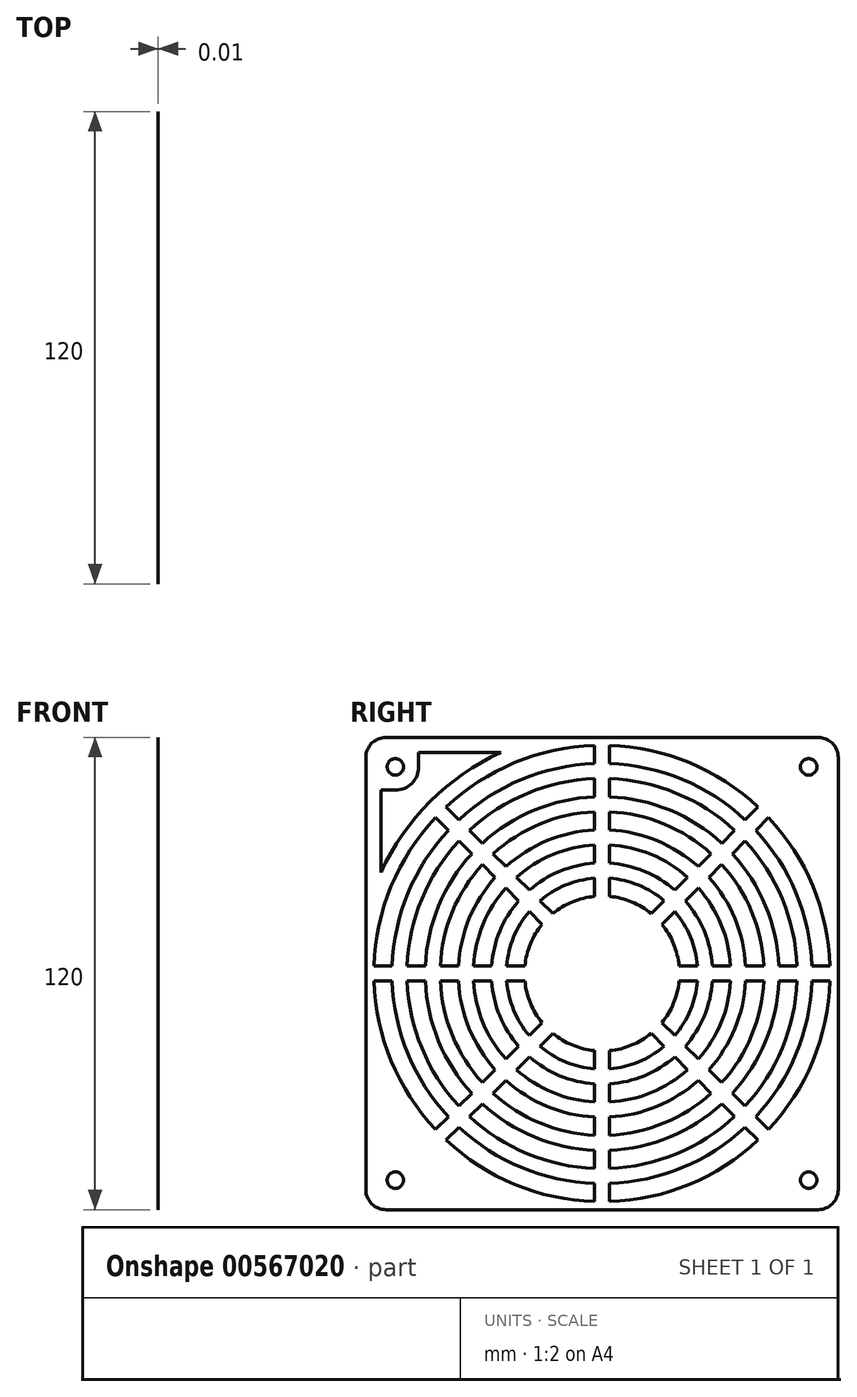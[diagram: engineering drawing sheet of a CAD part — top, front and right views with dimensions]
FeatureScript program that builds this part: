
annotation { "Feature Type Name" : "Feature", "Feature Type Description" : "" }
export const myFeature = defineFeature(function(context is Context, id is Id, definition is map)
    precondition{}
    {
        {
            var Q0;
            Q0=qCreatedBy(makeId("Right.planeOp"),FACE);
            var sketch = newSketch(context, id + "F0", { "sketchPlane" : qUnion([Q0])});
            skLineSegment(sketch, "E0.bottom", {"start": v(-54.92, 60) * mm, "end": v(54.92, 60) * mm});
            skLineSegment(sketch, "E0.top", {"start": v(-54.92, -60) * mm, "end": v(54.92, -60) * mm});
            skLineSegment(sketch, "E0.left", {"start": v(-60, 54.92) * mm, "end": v(-60, -54.92) * mm});
            skLineSegment(sketch, "E0.right", {"start": v(60, 54.92) * mm, "end": v(60, -54.92) * mm});
            skPoint(sketch, "E0.middle", {"position": v(0, 0) * mm});
            skPoint(sketch, "E1.visualSharp", {"position": v(-60, 60) * mm});
            skArc(sketch, "E1.filletArc", {"start": v(-54.92, 60) * mm, "mid": v(-58.51, 58.51) * mm, "end": v(-60, 54.92) * mm});
            skPoint(sketch, "E2.visualSharp", {"position": v(60, 60) * mm});
            skArc(sketch, "E2.filletArc", {"start": v(60, 54.92) * mm, "mid": v(58.51, 58.51) * mm, "end": v(54.92, 60) * mm});
            skPoint(sketch, "E3.visualSharp", {"position": v(60, -60) * mm});
            skArc(sketch, "E3.filletArc", {"start": v(54.92, -60) * mm, "mid": v(58.51, -58.51) * mm, "end": v(60, -54.92) * mm});
            skPoint(sketch, "E4.visualSharp", {"position": v(-60, -60) * mm});
            skArc(sketch, "E4.filletArc", {"start": v(-60, -54.92) * mm, "mid": v(-58.51, -58.51) * mm, "end": v(-54.92, -60) * mm});
            skLineSegment(sketch, "E5.bottom", {"start": v(-52.5, 52.5) * mm, "end": v(52.5, 52.5) * mm, "construction": true});
            skLineSegment(sketch, "E5.top", {"start": v(-52.5, -52.5) * mm, "end": v(52.5, -52.5) * mm, "construction": true});
            skLineSegment(sketch, "E5.left", {"start": v(-52.5, 52.5) * mm, "end": v(-52.5, -52.5) * mm, "construction": true});
            skLineSegment(sketch, "E5.right", {"start": v(52.5, 52.5) * mm, "end": v(52.5, -52.5) * mm, "construction": true});
            skCircle(sketch, "E6", {"center": v(-52.5, 52.5) * mm, "radius": 2.1 * mm});
            skCircle(sketch, "E7", {"center": v(52.5, 52.5) * mm, "radius": 2.1 * mm});
            skCircle(sketch, "E8", {"center": v(52.5, -52.5) * mm, "radius": 2.1 * mm});
            skCircle(sketch, "E9", {"center": v(-52.5, -52.5) * mm, "radius": 2.1 * mm});
            skCircle(sketch, "E10", {"center": v(0, 0) * mm, "radius": 57.98 * mm});
            skCircle(sketch, "E11", {"center": v(0, 0) * mm, "radius": 19.69 * mm});
            skCircle(sketch, "E12", {"center": v(0, 0) * mm, "radius": 24.3 * mm});
            skCircle(sketch, "E13", {"center": v(0, 0) * mm, "radius": 28.1 * mm});
            skCircle(sketch, "E14", {"center": v(0, 0) * mm, "radius": 32.72 * mm});
            skCircle(sketch, "E15", {"center": v(0, 0) * mm, "radius": 36.53 * mm});
            skCircle(sketch, "E16", {"center": v(0, 0) * mm, "radius": 41.14 * mm});
            skCircle(sketch, "E17", {"center": v(0, 0) * mm, "radius": 44.95 * mm});
            skLineSegment(sketch, "E18", {"start": v(0, 19.69) * mm, "end": v(0, 24.3) * mm, "construction": true});
            skLineSegment(sketch, "E19", {"start": v(0, 24.3) * mm, "end": v(0, 28.1) * mm, "construction": true});
            skLineSegment(sketch, "E20", {"start": v(0, 28.1) * mm, "end": v(0, 32.72) * mm, "construction": true});
            skLineSegment(sketch, "E21", {"start": v(0, 32.72) * mm, "end": v(0, 36.53) * mm, "construction": true});
            skLineSegment(sketch, "E22", {"start": v(0, 36.53) * mm, "end": v(0, 41.14) * mm, "construction": true});
            skLineSegment(sketch, "E23", {"start": v(0, 41.14) * mm, "end": v(0, 44.95) * mm, "construction": true});
            skCircle(sketch, "E24", {"center": v(0, 0) * mm, "radius": 49.56 * mm});
            skCircle(sketch, "E25", {"center": v(0, 0) * mm, "radius": 53.37 * mm});
            skLineSegment(sketch, "E26", {"start": v(0, 44.95) * mm, "end": v(0, 49.56) * mm, "construction": true});
            skLineSegment(sketch, "E27", {"start": v(0, 49.56) * mm, "end": v(0, 53.37) * mm, "construction": true});
            skLineSegment(sketch, "E28", {"start": v(0, 53.37) * mm, "end": v(0, 57.98) * mm, "construction": true});
            skLineSegment(sketch, "E29", {"start": v(-19.6, 1.9) * mm, "end": v(-57.94, 1.9) * mm});
            skLineSegment(sketch, "E30", {"start": v(-57.94, -1.9) * mm, "end": v(-19.6, -1.9) * mm});
            skLineSegment(sketch, "E31", {"start": v(-38.77, 1.9) * mm, "end": v(-38.77, -1.9) * mm, "construction": true});
            skLineSegment(sketch, "E32", {"start": v(-38.77, 0) * mm, "end": v(0, 0) * mm, "construction": true});
            skLineSegment(sketch, "E33.1.0", {"start": v(-15.2, -12.5) * mm, "end": v(-42.32, -39.63) * mm});
            skLineSegment(sketch, "E33.1.1", {"start": v(-39.63, -42.32) * mm, "end": v(-12.5, -15.2) * mm});
            skLineSegment(sketch, "E33.2.0", {"start": v(-1.9, -19.6) * mm, "end": v(-1.9, -57.94) * mm});
            skLineSegment(sketch, "E33.2.1", {"start": v(1.9, -57.94) * mm, "end": v(1.9, -19.6) * mm});
            skLineSegment(sketch, "E33.3.0", {"start": v(12.5, -15.2) * mm, "end": v(39.63, -42.32) * mm});
            skLineSegment(sketch, "E33.3.1", {"start": v(42.32, -39.63) * mm, "end": v(15.2, -12.5) * mm});
            skLineSegment(sketch, "E33.4.0", {"start": v(19.6, -1.9) * mm, "end": v(57.94, -1.9) * mm});
            skLineSegment(sketch, "E33.4.1", {"start": v(57.94, 1.9) * mm, "end": v(19.6, 1.9) * mm});
            skLineSegment(sketch, "E33.5.0", {"start": v(15.2, 12.5) * mm, "end": v(42.32, 39.63) * mm});
            skLineSegment(sketch, "E33.5.1", {"start": v(39.63, 42.32) * mm, "end": v(12.5, 15.2) * mm});
            skLineSegment(sketch, "E33.6.0", {"start": v(1.9, 19.6) * mm, "end": v(1.9, 57.94) * mm});
            skLineSegment(sketch, "E33.6.1", {"start": v(-1.9, 57.94) * mm, "end": v(-1.9, 19.6) * mm});
            skLineSegment(sketch, "E33.7.0", {"start": v(-12.5, 15.2) * mm, "end": v(-39.63, 42.32) * mm});
            skLineSegment(sketch, "E33.7.1", {"start": v(-42.32, 39.63) * mm, "end": v(-15.2, 12.5) * mm});
            skSolve(sketch);
        }
        {
            var Q0;
            {var subQ0=sQuery(id+"F0.wireOp",EDGE,"E33.1.0");var subQ1=sQuery(id+"F0.wireOp",EDGE,"E11");var subQ2=makeQuery(id+"F0.imprint","INTERSECT",VERTEX,{"derivedFrom":[subQ1,subQ0]});Q0=makeQuery(id+"F0.imprint","IMPRINT",FACE,{"disambiguationData":[TD([[makeQuery(id+"F0.imprint","IMPRINT",EDGE,{"disambiguationData":[TD([[subQ2,-1.0]])],"derivedFrom":subQ1}),-1.0]])]});}
            var Q1;
            {var subQ0=sQuery(id+"F0.wireOp",EDGE,"E11");var subQ8=makeQuery(id+"F0.imprint","INTERSECT",VERTEX,{"derivedFrom":[subQ0,sQuery(id+"F0.wireOp",EDGE,"E33.4.1")]});Q1=makeQuery(id+"F0.imprint","IMPRINT",FACE,{"disambiguationData":[TD([[makeQuery(id+"F0.imprint","IMPRINT",EDGE,{"disambiguationData":[TD([[subQ8,-1.0]])],"derivedFrom":subQ0}),1.0]])]});}
            var Q2;
            {var subQ0=sQuery(id+"F0.wireOp",EDGE,"E33.1.0");var subQ1=sQuery(id+"F0.wireOp",EDGE,"E12");var subQ2=makeQuery(id+"F0.imprint","INTERSECT",VERTEX,{"derivedFrom":[subQ1,subQ0]});Q2=makeQuery(id+"F0.imprint","IMPRINT",FACE,{"disambiguationData":[TD([[makeQuery(id+"F0.imprint","IMPRINT",EDGE,{"disambiguationData":[TD([[subQ2,-1.0]])],"derivedFrom":subQ1}),-1.0]])]});}
            var Q3;
            {var subQ0=sQuery(id+"F0.wireOp",EDGE,"E33.1.0");var subQ1=sQuery(id+"F0.wireOp",EDGE,"E13");var subQ2=makeQuery(id+"F0.imprint","INTERSECT",VERTEX,{"derivedFrom":[subQ1,subQ0]});Q3=makeQuery(id+"F0.imprint","IMPRINT",FACE,{"disambiguationData":[TD([[makeQuery(id+"F0.imprint","IMPRINT",EDGE,{"disambiguationData":[TD([[subQ2,-1.0]])],"derivedFrom":subQ1}),-1.0]])]});}
            var Q4;
            {var subQ0=sQuery(id+"F0.wireOp",EDGE,"E33.1.0");var subQ1=sQuery(id+"F0.wireOp",EDGE,"E14");var subQ2=makeQuery(id+"F0.imprint","INTERSECT",VERTEX,{"derivedFrom":[subQ1,subQ0]});Q4=makeQuery(id+"F0.imprint","IMPRINT",FACE,{"disambiguationData":[TD([[makeQuery(id+"F0.imprint","IMPRINT",EDGE,{"disambiguationData":[TD([[subQ2,-1.0]])],"derivedFrom":subQ1}),-1.0]])]});}
            var Q5;
            {var subQ0=sQuery(id+"F0.wireOp",EDGE,"E33.1.0");var subQ1=sQuery(id+"F0.wireOp",EDGE,"E15");var subQ2=makeQuery(id+"F0.imprint","INTERSECT",VERTEX,{"derivedFrom":[subQ1,subQ0]});Q5=makeQuery(id+"F0.imprint","IMPRINT",FACE,{"disambiguationData":[TD([[makeQuery(id+"F0.imprint","IMPRINT",EDGE,{"disambiguationData":[TD([[subQ2,-1.0]])],"derivedFrom":subQ1}),-1.0]])]});}
            var Q6;
            {var subQ0=sQuery(id+"F0.wireOp",EDGE,"E33.1.0");var subQ1=sQuery(id+"F0.wireOp",EDGE,"E16");var subQ2=makeQuery(id+"F0.imprint","INTERSECT",VERTEX,{"derivedFrom":[subQ1,subQ0]});Q6=makeQuery(id+"F0.imprint","IMPRINT",FACE,{"disambiguationData":[TD([[makeQuery(id+"F0.imprint","IMPRINT",EDGE,{"disambiguationData":[TD([[subQ2,-1.0]])],"derivedFrom":subQ1}),-1.0]])]});}
            var Q7;
            {var subQ0=sQuery(id+"F0.wireOp",EDGE,"E33.1.0");var subQ1=sQuery(id+"F0.wireOp",EDGE,"E17");var subQ2=makeQuery(id+"F0.imprint","INTERSECT",VERTEX,{"derivedFrom":[subQ1,subQ0]});Q7=makeQuery(id+"F0.imprint","IMPRINT",FACE,{"disambiguationData":[TD([[makeQuery(id+"F0.imprint","IMPRINT",EDGE,{"disambiguationData":[TD([[subQ2,-1.0]])],"derivedFrom":subQ1}),-1.0]])]});}
            var Q8;
            {var subQ0=sQuery(id+"F0.wireOp",EDGE,"E33.1.0");var subQ1=sQuery(id+"F0.wireOp",EDGE,"E24");var subQ2=makeQuery(id+"F0.imprint","INTERSECT",VERTEX,{"derivedFrom":[subQ1,subQ0]});Q8=makeQuery(id+"F0.imprint","IMPRINT",FACE,{"disambiguationData":[TD([[makeQuery(id+"F0.imprint","IMPRINT",EDGE,{"disambiguationData":[TD([[subQ2,-1.0]])],"derivedFrom":subQ1}),-1.0]])]});}
            var Q9;
            {var subQ0=sQuery(id+"F0.wireOp",EDGE,"E33.1.0");var subQ1=sQuery(id+"F0.wireOp",EDGE,"E10");var subQ2=makeQuery(id+"F0.imprint","INTERSECT",VERTEX,{"derivedFrom":[subQ1,subQ0]});Q9=makeQuery(id+"F0.imprint","IMPRINT",FACE,{"disambiguationData":[TD([[makeQuery(id+"F0.imprint","IMPRINT",EDGE,{"disambiguationData":[TD([[subQ2,-1.0]])],"derivedFrom":subQ1}),1.0]])]});}
            var Q10;
            Q10=makeQuery(id+"F0.imprint","IMPRINT",FACE,{"disambiguationData":[TD([[makeQuery(id+"F0.imprint","IMPRINT",EDGE,{"derivedFrom":sQuery(id+"F0.wireOp",EDGE,"E0.bottom")}),-1.0]])]});
            var Q11;
            {var subQ0=sQuery(id+"F0.wireOp",EDGE,"E33.2.0");var subQ1=sQuery(id+"F0.wireOp",EDGE,"E10");var subQ2=makeQuery(id+"F0.imprint","INTERSECT",VERTEX,{"derivedFrom":[subQ1,subQ0]});Q11=makeQuery(id+"F0.imprint","IMPRINT",FACE,{"disambiguationData":[TD([[makeQuery(id+"F0.imprint","IMPRINT",EDGE,{"disambiguationData":[TD([[subQ2,-1.0]])],"derivedFrom":subQ1}),1.0]])]});}
            var Q12;
            {var subQ0=sQuery(id+"F0.wireOp",EDGE,"E33.2.0");var subQ1=sQuery(id+"F0.wireOp",EDGE,"E24");var subQ2=makeQuery(id+"F0.imprint","INTERSECT",VERTEX,{"derivedFrom":[subQ1,subQ0]});Q12=makeQuery(id+"F0.imprint","IMPRINT",FACE,{"disambiguationData":[TD([[makeQuery(id+"F0.imprint","IMPRINT",EDGE,{"disambiguationData":[TD([[subQ2,-1.0]])],"derivedFrom":subQ1}),-1.0]])]});}
            var Q13;
            {var subQ0=sQuery(id+"F0.wireOp",EDGE,"E33.2.0");var subQ1=sQuery(id+"F0.wireOp",EDGE,"E17");var subQ2=makeQuery(id+"F0.imprint","INTERSECT",VERTEX,{"derivedFrom":[subQ1,subQ0]});Q13=makeQuery(id+"F0.imprint","IMPRINT",FACE,{"disambiguationData":[TD([[makeQuery(id+"F0.imprint","IMPRINT",EDGE,{"disambiguationData":[TD([[subQ2,-1.0]])],"derivedFrom":subQ1}),-1.0]])]});}
            var Q14;
            {var subQ0=sQuery(id+"F0.wireOp",EDGE,"E33.2.0");var subQ1=sQuery(id+"F0.wireOp",EDGE,"E16");var subQ2=makeQuery(id+"F0.imprint","INTERSECT",VERTEX,{"derivedFrom":[subQ1,subQ0]});Q14=makeQuery(id+"F0.imprint","IMPRINT",FACE,{"disambiguationData":[TD([[makeQuery(id+"F0.imprint","IMPRINT",EDGE,{"disambiguationData":[TD([[subQ2,-1.0]])],"derivedFrom":subQ1}),-1.0]])]});}
            var Q15;
            {var subQ0=sQuery(id+"F0.wireOp",EDGE,"E33.2.0");var subQ1=sQuery(id+"F0.wireOp",EDGE,"E15");var subQ2=makeQuery(id+"F0.imprint","INTERSECT",VERTEX,{"derivedFrom":[subQ1,subQ0]});Q15=makeQuery(id+"F0.imprint","IMPRINT",FACE,{"disambiguationData":[TD([[makeQuery(id+"F0.imprint","IMPRINT",EDGE,{"disambiguationData":[TD([[subQ2,-1.0]])],"derivedFrom":subQ1}),-1.0]])]});}
            var Q16;
            {var subQ0=sQuery(id+"F0.wireOp",EDGE,"E33.2.0");var subQ1=sQuery(id+"F0.wireOp",EDGE,"E14");var subQ2=makeQuery(id+"F0.imprint","INTERSECT",VERTEX,{"derivedFrom":[subQ1,subQ0]});Q16=makeQuery(id+"F0.imprint","IMPRINT",FACE,{"disambiguationData":[TD([[makeQuery(id+"F0.imprint","IMPRINT",EDGE,{"disambiguationData":[TD([[subQ2,-1.0]])],"derivedFrom":subQ1}),-1.0]])]});}
            var Q17;
            {var subQ0=sQuery(id+"F0.wireOp",EDGE,"E33.2.0");var subQ1=sQuery(id+"F0.wireOp",EDGE,"E13");var subQ2=makeQuery(id+"F0.imprint","INTERSECT",VERTEX,{"derivedFrom":[subQ1,subQ0]});Q17=makeQuery(id+"F0.imprint","IMPRINT",FACE,{"disambiguationData":[TD([[makeQuery(id+"F0.imprint","IMPRINT",EDGE,{"disambiguationData":[TD([[subQ2,-1.0]])],"derivedFrom":subQ1}),-1.0]])]});}
            var Q18;
            {var subQ0=sQuery(id+"F0.wireOp",EDGE,"E33.2.0");var subQ1=sQuery(id+"F0.wireOp",EDGE,"E12");var subQ2=makeQuery(id+"F0.imprint","INTERSECT",VERTEX,{"derivedFrom":[subQ1,subQ0]});Q18=makeQuery(id+"F0.imprint","IMPRINT",FACE,{"disambiguationData":[TD([[makeQuery(id+"F0.imprint","IMPRINT",EDGE,{"disambiguationData":[TD([[subQ2,-1.0]])],"derivedFrom":subQ1}),-1.0]])]});}
            var Q19;
            {var subQ0=sQuery(id+"F0.wireOp",EDGE,"E33.2.0");var subQ1=sQuery(id+"F0.wireOp",EDGE,"E11");var subQ2=makeQuery(id+"F0.imprint","INTERSECT",VERTEX,{"derivedFrom":[subQ1,subQ0]});Q19=makeQuery(id+"F0.imprint","IMPRINT",FACE,{"disambiguationData":[TD([[makeQuery(id+"F0.imprint","IMPRINT",EDGE,{"disambiguationData":[TD([[subQ2,-1.0]])],"derivedFrom":subQ1}),-1.0]])]});}
            var Q20;
            {var subQ0=sQuery(id+"F0.wireOp",EDGE,"E33.1.1");var subQ1=sQuery(id+"F0.wireOp",EDGE,"E12");var subQ2=makeQuery(id+"F0.imprint","INTERSECT",VERTEX,{"derivedFrom":[subQ1,subQ0]});Q20=makeQuery(id+"F0.imprint","IMPRINT",FACE,{"disambiguationData":[TD([[makeQuery(id+"F0.imprint","IMPRINT",EDGE,{"disambiguationData":[TD([[subQ2,-1.0]])],"derivedFrom":subQ1}),-1.0]])]});}
            var Q21;
            {var subQ0=sQuery(id+"F0.wireOp",EDGE,"E33.1.1");var subQ1=sQuery(id+"F0.wireOp",EDGE,"E14");var subQ2=makeQuery(id+"F0.imprint","INTERSECT",VERTEX,{"derivedFrom":[subQ1,subQ0]});Q21=makeQuery(id+"F0.imprint","IMPRINT",FACE,{"disambiguationData":[TD([[makeQuery(id+"F0.imprint","IMPRINT",EDGE,{"disambiguationData":[TD([[subQ2,-1.0]])],"derivedFrom":subQ1}),-1.0]])]});}
            var Q22;
            {var subQ0=sQuery(id+"F0.wireOp",EDGE,"E33.1.1");var subQ1=sQuery(id+"F0.wireOp",EDGE,"E16");var subQ2=makeQuery(id+"F0.imprint","INTERSECT",VERTEX,{"derivedFrom":[subQ1,subQ0]});Q22=makeQuery(id+"F0.imprint","IMPRINT",FACE,{"disambiguationData":[TD([[makeQuery(id+"F0.imprint","IMPRINT",EDGE,{"disambiguationData":[TD([[subQ2,-1.0]])],"derivedFrom":subQ1}),-1.0]])]});}
            var Q23;
            {var subQ0=sQuery(id+"F0.wireOp",EDGE,"E33.1.1");var subQ1=sQuery(id+"F0.wireOp",EDGE,"E24");var subQ2=makeQuery(id+"F0.imprint","INTERSECT",VERTEX,{"derivedFrom":[subQ1,subQ0]});Q23=makeQuery(id+"F0.imprint","IMPRINT",FACE,{"disambiguationData":[TD([[makeQuery(id+"F0.imprint","IMPRINT",EDGE,{"disambiguationData":[TD([[subQ2,-1.0]])],"derivedFrom":subQ1}),-1.0]])]});}
            var Q24;
            {var subQ0=sQuery(id+"F0.wireOp",EDGE,"E33.2.1");var subQ1=sQuery(id+"F0.wireOp",EDGE,"E24");var subQ2=makeQuery(id+"F0.imprint","INTERSECT",VERTEX,{"derivedFrom":[subQ1,subQ0]});Q24=makeQuery(id+"F0.imprint","IMPRINT",FACE,{"disambiguationData":[TD([[makeQuery(id+"F0.imprint","IMPRINT",EDGE,{"disambiguationData":[TD([[subQ2,-1.0]])],"derivedFrom":subQ1}),-1.0]])]});}
            var Q25;
            {var subQ0=sQuery(id+"F0.wireOp",EDGE,"E33.2.1");var subQ1=sQuery(id+"F0.wireOp",EDGE,"E16");var subQ2=makeQuery(id+"F0.imprint","INTERSECT",VERTEX,{"derivedFrom":[subQ1,subQ0]});Q25=makeQuery(id+"F0.imprint","IMPRINT",FACE,{"disambiguationData":[TD([[makeQuery(id+"F0.imprint","IMPRINT",EDGE,{"disambiguationData":[TD([[subQ2,-1.0]])],"derivedFrom":subQ1}),-1.0]])]});}
            var Q26;
            {var subQ0=sQuery(id+"F0.wireOp",EDGE,"E33.2.1");var subQ1=sQuery(id+"F0.wireOp",EDGE,"E14");var subQ2=makeQuery(id+"F0.imprint","INTERSECT",VERTEX,{"derivedFrom":[subQ1,subQ0]});Q26=makeQuery(id+"F0.imprint","IMPRINT",FACE,{"disambiguationData":[TD([[makeQuery(id+"F0.imprint","IMPRINT",EDGE,{"disambiguationData":[TD([[subQ2,-1.0]])],"derivedFrom":subQ1}),-1.0]])]});}
            var Q27;
            {var subQ0=sQuery(id+"F0.wireOp",EDGE,"E33.2.1");var subQ1=sQuery(id+"F0.wireOp",EDGE,"E12");var subQ2=makeQuery(id+"F0.imprint","INTERSECT",VERTEX,{"derivedFrom":[subQ1,subQ0]});Q27=makeQuery(id+"F0.imprint","IMPRINT",FACE,{"disambiguationData":[TD([[makeQuery(id+"F0.imprint","IMPRINT",EDGE,{"disambiguationData":[TD([[subQ2,-1.0]])],"derivedFrom":subQ1}),-1.0]])]});}
            var Q28;
            {var subQ0=sQuery(id+"F0.wireOp",EDGE,"E33.3.0");var subQ1=sQuery(id+"F0.wireOp",EDGE,"E12");var subQ2=makeQuery(id+"F0.imprint","INTERSECT",VERTEX,{"derivedFrom":[subQ1,subQ0]});Q28=makeQuery(id+"F0.imprint","IMPRINT",FACE,{"disambiguationData":[TD([[makeQuery(id+"F0.imprint","IMPRINT",EDGE,{"disambiguationData":[TD([[subQ2,-1.0]])],"derivedFrom":subQ1}),-1.0]])]});}
            var Q29;
            {var subQ0=sQuery(id+"F0.wireOp",EDGE,"E33.3.0");var subQ1=sQuery(id+"F0.wireOp",EDGE,"E11");var subQ2=makeQuery(id+"F0.imprint","INTERSECT",VERTEX,{"derivedFrom":[subQ1,subQ0]});Q29=makeQuery(id+"F0.imprint","IMPRINT",FACE,{"disambiguationData":[TD([[makeQuery(id+"F0.imprint","IMPRINT",EDGE,{"disambiguationData":[TD([[subQ2,-1.0]])],"derivedFrom":subQ1}),-1.0]])]});}
            var Q30;
            {var subQ0=sQuery(id+"F0.wireOp",EDGE,"E33.3.0");var subQ1=sQuery(id+"F0.wireOp",EDGE,"E13");var subQ2=makeQuery(id+"F0.imprint","INTERSECT",VERTEX,{"derivedFrom":[subQ1,subQ0]});Q30=makeQuery(id+"F0.imprint","IMPRINT",FACE,{"disambiguationData":[TD([[makeQuery(id+"F0.imprint","IMPRINT",EDGE,{"disambiguationData":[TD([[subQ2,-1.0]])],"derivedFrom":subQ1}),-1.0]])]});}
            var Q31;
            {var subQ0=sQuery(id+"F0.wireOp",EDGE,"E33.3.0");var subQ1=sQuery(id+"F0.wireOp",EDGE,"E14");var subQ2=makeQuery(id+"F0.imprint","INTERSECT",VERTEX,{"derivedFrom":[subQ1,subQ0]});Q31=makeQuery(id+"F0.imprint","IMPRINT",FACE,{"disambiguationData":[TD([[makeQuery(id+"F0.imprint","IMPRINT",EDGE,{"disambiguationData":[TD([[subQ2,-1.0]])],"derivedFrom":subQ1}),-1.0]])]});}
            var Q32;
            {var subQ0=sQuery(id+"F0.wireOp",EDGE,"E33.3.0");var subQ1=sQuery(id+"F0.wireOp",EDGE,"E15");var subQ2=makeQuery(id+"F0.imprint","INTERSECT",VERTEX,{"derivedFrom":[subQ1,subQ0]});Q32=makeQuery(id+"F0.imprint","IMPRINT",FACE,{"disambiguationData":[TD([[makeQuery(id+"F0.imprint","IMPRINT",EDGE,{"disambiguationData":[TD([[subQ2,-1.0]])],"derivedFrom":subQ1}),-1.0]])]});}
            var Q33;
            {var subQ0=sQuery(id+"F0.wireOp",EDGE,"E33.3.0");var subQ1=sQuery(id+"F0.wireOp",EDGE,"E16");var subQ2=makeQuery(id+"F0.imprint","INTERSECT",VERTEX,{"derivedFrom":[subQ1,subQ0]});Q33=makeQuery(id+"F0.imprint","IMPRINT",FACE,{"disambiguationData":[TD([[makeQuery(id+"F0.imprint","IMPRINT",EDGE,{"disambiguationData":[TD([[subQ2,-1.0]])],"derivedFrom":subQ1}),-1.0]])]});}
            var Q34;
            {var subQ0=sQuery(id+"F0.wireOp",EDGE,"E33.3.0");var subQ1=sQuery(id+"F0.wireOp",EDGE,"E17");var subQ2=makeQuery(id+"F0.imprint","INTERSECT",VERTEX,{"derivedFrom":[subQ1,subQ0]});Q34=makeQuery(id+"F0.imprint","IMPRINT",FACE,{"disambiguationData":[TD([[makeQuery(id+"F0.imprint","IMPRINT",EDGE,{"disambiguationData":[TD([[subQ2,-1.0]])],"derivedFrom":subQ1}),-1.0]])]});}
            var Q35;
            {var subQ0=sQuery(id+"F0.wireOp",EDGE,"E33.3.0");var subQ1=sQuery(id+"F0.wireOp",EDGE,"E24");var subQ2=makeQuery(id+"F0.imprint","INTERSECT",VERTEX,{"derivedFrom":[subQ1,subQ0]});Q35=makeQuery(id+"F0.imprint","IMPRINT",FACE,{"disambiguationData":[TD([[makeQuery(id+"F0.imprint","IMPRINT",EDGE,{"disambiguationData":[TD([[subQ2,-1.0]])],"derivedFrom":subQ1}),-1.0]])]});}
            var Q36;
            {var subQ0=sQuery(id+"F0.wireOp",EDGE,"E33.3.0");var subQ1=sQuery(id+"F0.wireOp",EDGE,"E10");var subQ2=makeQuery(id+"F0.imprint","INTERSECT",VERTEX,{"derivedFrom":[subQ1,subQ0]});Q36=makeQuery(id+"F0.imprint","IMPRINT",FACE,{"disambiguationData":[TD([[makeQuery(id+"F0.imprint","IMPRINT",EDGE,{"disambiguationData":[TD([[subQ2,-1.0]])],"derivedFrom":subQ1}),1.0]])]});}
            var Q37;
            {var subQ0=sQuery(id+"F0.wireOp",EDGE,"E33.3.1");var subQ1=sQuery(id+"F0.wireOp",EDGE,"E24");var subQ2=makeQuery(id+"F0.imprint","INTERSECT",VERTEX,{"derivedFrom":[subQ1,subQ0]});Q37=makeQuery(id+"F0.imprint","IMPRINT",FACE,{"disambiguationData":[TD([[makeQuery(id+"F0.imprint","IMPRINT",EDGE,{"disambiguationData":[TD([[subQ2,-1.0]])],"derivedFrom":subQ1}),-1.0]])]});}
            var Q38;
            {var subQ0=sQuery(id+"F0.wireOp",EDGE,"E33.3.1");var subQ1=sQuery(id+"F0.wireOp",EDGE,"E16");var subQ2=makeQuery(id+"F0.imprint","INTERSECT",VERTEX,{"derivedFrom":[subQ1,subQ0]});Q38=makeQuery(id+"F0.imprint","IMPRINT",FACE,{"disambiguationData":[TD([[makeQuery(id+"F0.imprint","IMPRINT",EDGE,{"disambiguationData":[TD([[subQ2,-1.0]])],"derivedFrom":subQ1}),-1.0]])]});}
            var Q39;
            {var subQ0=sQuery(id+"F0.wireOp",EDGE,"E33.3.1");var subQ1=sQuery(id+"F0.wireOp",EDGE,"E14");var subQ2=makeQuery(id+"F0.imprint","INTERSECT",VERTEX,{"derivedFrom":[subQ1,subQ0]});Q39=makeQuery(id+"F0.imprint","IMPRINT",FACE,{"disambiguationData":[TD([[makeQuery(id+"F0.imprint","IMPRINT",EDGE,{"disambiguationData":[TD([[subQ2,-1.0]])],"derivedFrom":subQ1}),-1.0]])]});}
            var Q40;
            {var subQ0=sQuery(id+"F0.wireOp",EDGE,"E33.3.1");var subQ1=sQuery(id+"F0.wireOp",EDGE,"E12");var subQ2=makeQuery(id+"F0.imprint","INTERSECT",VERTEX,{"derivedFrom":[subQ1,subQ0]});Q40=makeQuery(id+"F0.imprint","IMPRINT",FACE,{"disambiguationData":[TD([[makeQuery(id+"F0.imprint","IMPRINT",EDGE,{"disambiguationData":[TD([[subQ2,-1.0]])],"derivedFrom":subQ1}),-1.0]])]});}
            var Q41;
            {var subQ0=sQuery(id+"F0.wireOp",EDGE,"E33.4.0");var subQ1=sQuery(id+"F0.wireOp",EDGE,"E11");var subQ2=makeQuery(id+"F0.imprint","INTERSECT",VERTEX,{"derivedFrom":[subQ1,subQ0]});Q41=makeQuery(id+"F0.imprint","IMPRINT",FACE,{"disambiguationData":[TD([[makeQuery(id+"F0.imprint","IMPRINT",EDGE,{"disambiguationData":[TD([[subQ2,-1.0]])],"derivedFrom":subQ1}),-1.0]])]});}
            var Q42;
            {var subQ0=sQuery(id+"F0.wireOp",EDGE,"E33.4.1");var subQ1=sQuery(id+"F0.wireOp",EDGE,"E12");var subQ2=makeQuery(id+"F0.imprint","INTERSECT",VERTEX,{"derivedFrom":[subQ1,subQ0]});Q42=makeQuery(id+"F0.imprint","IMPRINT",FACE,{"disambiguationData":[TD([[makeQuery(id+"F0.imprint","IMPRINT",EDGE,{"disambiguationData":[TD([[subQ2,1.0]])],"derivedFrom":subQ1}),-1.0]])]});}
            var Q43;
            {var subQ0=sQuery(id+"F0.wireOp",EDGE,"E33.4.1");var subQ1=sQuery(id+"F0.wireOp",EDGE,"E13");var subQ2=makeQuery(id+"F0.imprint","INTERSECT",VERTEX,{"derivedFrom":[subQ1,subQ0]});Q43=makeQuery(id+"F0.imprint","IMPRINT",FACE,{"disambiguationData":[TD([[makeQuery(id+"F0.imprint","IMPRINT",EDGE,{"disambiguationData":[TD([[subQ2,1.0]])],"derivedFrom":subQ1}),-1.0]])]});}
            var Q44;
            {var subQ0=sQuery(id+"F0.wireOp",EDGE,"E33.4.1");var subQ1=sQuery(id+"F0.wireOp",EDGE,"E14");var subQ2=makeQuery(id+"F0.imprint","INTERSECT",VERTEX,{"derivedFrom":[subQ1,subQ0]});Q44=makeQuery(id+"F0.imprint","IMPRINT",FACE,{"disambiguationData":[TD([[makeQuery(id+"F0.imprint","IMPRINT",EDGE,{"disambiguationData":[TD([[subQ2,1.0]])],"derivedFrom":subQ1}),-1.0]])]});}
            var Q45;
            {var subQ0=sQuery(id+"F0.wireOp",EDGE,"E33.4.1");var subQ1=sQuery(id+"F0.wireOp",EDGE,"E15");var subQ2=makeQuery(id+"F0.imprint","INTERSECT",VERTEX,{"derivedFrom":[subQ1,subQ0]});Q45=makeQuery(id+"F0.imprint","IMPRINT",FACE,{"disambiguationData":[TD([[makeQuery(id+"F0.imprint","IMPRINT",EDGE,{"disambiguationData":[TD([[subQ2,1.0]])],"derivedFrom":subQ1}),-1.0]])]});}
            var Q46;
            {var subQ0=sQuery(id+"F0.wireOp",EDGE,"E33.4.1");var subQ1=sQuery(id+"F0.wireOp",EDGE,"E16");var subQ2=makeQuery(id+"F0.imprint","INTERSECT",VERTEX,{"derivedFrom":[subQ1,subQ0]});Q46=makeQuery(id+"F0.imprint","IMPRINT",FACE,{"disambiguationData":[TD([[makeQuery(id+"F0.imprint","IMPRINT",EDGE,{"disambiguationData":[TD([[subQ2,1.0]])],"derivedFrom":subQ1}),-1.0]])]});}
            var Q47;
            {var subQ0=sQuery(id+"F0.wireOp",EDGE,"E33.4.1");var subQ1=sQuery(id+"F0.wireOp",EDGE,"E17");var subQ2=makeQuery(id+"F0.imprint","INTERSECT",VERTEX,{"derivedFrom":[subQ1,subQ0]});Q47=makeQuery(id+"F0.imprint","IMPRINT",FACE,{"disambiguationData":[TD([[makeQuery(id+"F0.imprint","IMPRINT",EDGE,{"disambiguationData":[TD([[subQ2,1.0]])],"derivedFrom":subQ1}),-1.0]])]});}
            var Q48;
            {var subQ0=sQuery(id+"F0.wireOp",EDGE,"E33.4.1");var subQ1=sQuery(id+"F0.wireOp",EDGE,"E24");var subQ2=makeQuery(id+"F0.imprint","INTERSECT",VERTEX,{"derivedFrom":[subQ1,subQ0]});Q48=makeQuery(id+"F0.imprint","IMPRINT",FACE,{"disambiguationData":[TD([[makeQuery(id+"F0.imprint","IMPRINT",EDGE,{"disambiguationData":[TD([[subQ2,1.0]])],"derivedFrom":subQ1}),-1.0]])]});}
            var Q49;
            {var subQ0=sQuery(id+"F0.wireOp",EDGE,"E33.4.0");var subQ1=sQuery(id+"F0.wireOp",EDGE,"E10");var subQ2=makeQuery(id+"F0.imprint","INTERSECT",VERTEX,{"derivedFrom":[subQ1,subQ0]});Q49=makeQuery(id+"F0.imprint","IMPRINT",FACE,{"disambiguationData":[TD([[makeQuery(id+"F0.imprint","IMPRINT",EDGE,{"disambiguationData":[TD([[subQ2,-1.0]])],"derivedFrom":subQ1}),1.0]])]});}
            var Q50;
            {var subQ0=sQuery(id+"F0.wireOp",EDGE,"E33.5.0");var subQ1=sQuery(id+"F0.wireOp",EDGE,"E24");var subQ2=makeQuery(id+"F0.imprint","INTERSECT",VERTEX,{"derivedFrom":[subQ1,subQ0]});Q50=makeQuery(id+"F0.imprint","IMPRINT",FACE,{"disambiguationData":[TD([[makeQuery(id+"F0.imprint","IMPRINT",EDGE,{"disambiguationData":[TD([[subQ2,1.0]])],"derivedFrom":subQ1}),-1.0]])]});}
            var Q51;
            {var subQ0=sQuery(id+"F0.wireOp",EDGE,"E33.5.0");var subQ1=sQuery(id+"F0.wireOp",EDGE,"E16");var subQ2=makeQuery(id+"F0.imprint","INTERSECT",VERTEX,{"derivedFrom":[subQ1,subQ0]});Q51=makeQuery(id+"F0.imprint","IMPRINT",FACE,{"disambiguationData":[TD([[makeQuery(id+"F0.imprint","IMPRINT",EDGE,{"disambiguationData":[TD([[subQ2,1.0]])],"derivedFrom":subQ1}),-1.0]])]});}
            var Q52;
            {var subQ0=sQuery(id+"F0.wireOp",EDGE,"E33.5.0");var subQ1=sQuery(id+"F0.wireOp",EDGE,"E14");var subQ2=makeQuery(id+"F0.imprint","INTERSECT",VERTEX,{"derivedFrom":[subQ1,subQ0]});Q52=makeQuery(id+"F0.imprint","IMPRINT",FACE,{"disambiguationData":[TD([[makeQuery(id+"F0.imprint","IMPRINT",EDGE,{"disambiguationData":[TD([[subQ2,1.0]])],"derivedFrom":subQ1}),-1.0]])]});}
            var Q53;
            {var subQ0=sQuery(id+"F0.wireOp",EDGE,"E33.5.0");var subQ1=sQuery(id+"F0.wireOp",EDGE,"E12");var subQ2=makeQuery(id+"F0.imprint","INTERSECT",VERTEX,{"derivedFrom":[subQ1,subQ0]});Q53=makeQuery(id+"F0.imprint","IMPRINT",FACE,{"disambiguationData":[TD([[makeQuery(id+"F0.imprint","IMPRINT",EDGE,{"disambiguationData":[TD([[subQ2,1.0]])],"derivedFrom":subQ1}),-1.0]])]});}
            var Q54;
            {var subQ0=sQuery(id+"F0.wireOp",EDGE,"E33.5.0");var subQ1=sQuery(id+"F0.wireOp",EDGE,"E11");var subQ2=makeQuery(id+"F0.imprint","INTERSECT",VERTEX,{"derivedFrom":[subQ1,subQ0]});Q54=makeQuery(id+"F0.imprint","IMPRINT",FACE,{"disambiguationData":[TD([[makeQuery(id+"F0.imprint","IMPRINT",EDGE,{"disambiguationData":[TD([[subQ2,-1.0]])],"derivedFrom":subQ1}),-1.0]])]});}
            var Q55;
            {var subQ0=sQuery(id+"F0.wireOp",EDGE,"E33.5.0");var subQ1=sQuery(id+"F0.wireOp",EDGE,"E12");var subQ2=makeQuery(id+"F0.imprint","INTERSECT",VERTEX,{"derivedFrom":[subQ1,subQ0]});Q55=makeQuery(id+"F0.imprint","IMPRINT",FACE,{"disambiguationData":[TD([[makeQuery(id+"F0.imprint","IMPRINT",EDGE,{"disambiguationData":[TD([[subQ2,-1.0]])],"derivedFrom":subQ1}),-1.0]])]});}
            var Q56;
            {var subQ0=sQuery(id+"F0.wireOp",EDGE,"E33.5.0");var subQ1=sQuery(id+"F0.wireOp",EDGE,"E13");var subQ2=makeQuery(id+"F0.imprint","INTERSECT",VERTEX,{"derivedFrom":[subQ1,subQ0]});Q56=makeQuery(id+"F0.imprint","IMPRINT",FACE,{"disambiguationData":[TD([[makeQuery(id+"F0.imprint","IMPRINT",EDGE,{"disambiguationData":[TD([[subQ2,-1.0]])],"derivedFrom":subQ1}),-1.0]])]});}
            var Q57;
            {var subQ0=sQuery(id+"F0.wireOp",EDGE,"E33.5.0");var subQ1=sQuery(id+"F0.wireOp",EDGE,"E14");var subQ2=makeQuery(id+"F0.imprint","INTERSECT",VERTEX,{"derivedFrom":[subQ1,subQ0]});Q57=makeQuery(id+"F0.imprint","IMPRINT",FACE,{"disambiguationData":[TD([[makeQuery(id+"F0.imprint","IMPRINT",EDGE,{"disambiguationData":[TD([[subQ2,-1.0]])],"derivedFrom":subQ1}),-1.0]])]});}
            var Q58;
            {var subQ0=sQuery(id+"F0.wireOp",EDGE,"E33.5.0");var subQ1=sQuery(id+"F0.wireOp",EDGE,"E15");var subQ2=makeQuery(id+"F0.imprint","INTERSECT",VERTEX,{"derivedFrom":[subQ1,subQ0]});Q58=makeQuery(id+"F0.imprint","IMPRINT",FACE,{"disambiguationData":[TD([[makeQuery(id+"F0.imprint","IMPRINT",EDGE,{"disambiguationData":[TD([[subQ2,-1.0]])],"derivedFrom":subQ1}),-1.0]])]});}
            var Q59;
            {var subQ0=sQuery(id+"F0.wireOp",EDGE,"E33.5.0");var subQ1=sQuery(id+"F0.wireOp",EDGE,"E16");var subQ2=makeQuery(id+"F0.imprint","INTERSECT",VERTEX,{"derivedFrom":[subQ1,subQ0]});Q59=makeQuery(id+"F0.imprint","IMPRINT",FACE,{"disambiguationData":[TD([[makeQuery(id+"F0.imprint","IMPRINT",EDGE,{"disambiguationData":[TD([[subQ2,-1.0]])],"derivedFrom":subQ1}),-1.0]])]});}
            var Q60;
            {var subQ0=sQuery(id+"F0.wireOp",EDGE,"E33.5.0");var subQ1=sQuery(id+"F0.wireOp",EDGE,"E17");var subQ2=makeQuery(id+"F0.imprint","INTERSECT",VERTEX,{"derivedFrom":[subQ1,subQ0]});Q60=makeQuery(id+"F0.imprint","IMPRINT",FACE,{"disambiguationData":[TD([[makeQuery(id+"F0.imprint","IMPRINT",EDGE,{"disambiguationData":[TD([[subQ2,-1.0]])],"derivedFrom":subQ1}),-1.0]])]});}
            var Q61;
            {var subQ0=sQuery(id+"F0.wireOp",EDGE,"E33.5.0");var subQ1=sQuery(id+"F0.wireOp",EDGE,"E24");var subQ2=makeQuery(id+"F0.imprint","INTERSECT",VERTEX,{"derivedFrom":[subQ1,subQ0]});Q61=makeQuery(id+"F0.imprint","IMPRINT",FACE,{"disambiguationData":[TD([[makeQuery(id+"F0.imprint","IMPRINT",EDGE,{"disambiguationData":[TD([[subQ2,-1.0]])],"derivedFrom":subQ1}),-1.0]])]});}
            var Q62;
            {var subQ0=sQuery(id+"F0.wireOp",EDGE,"E33.5.0");var subQ1=sQuery(id+"F0.wireOp",EDGE,"E10");var subQ2=makeQuery(id+"F0.imprint","INTERSECT",VERTEX,{"derivedFrom":[subQ1,subQ0]});Q62=makeQuery(id+"F0.imprint","IMPRINT",FACE,{"disambiguationData":[TD([[makeQuery(id+"F0.imprint","IMPRINT",EDGE,{"disambiguationData":[TD([[subQ2,-1.0]])],"derivedFrom":subQ1}),1.0]])]});}
            var Q63;
            {var subQ0=sQuery(id+"F0.wireOp",EDGE,"E33.5.1");var subQ1=sQuery(id+"F0.wireOp",EDGE,"E12");var subQ2=makeQuery(id+"F0.imprint","INTERSECT",VERTEX,{"derivedFrom":[subQ1,subQ0]});Q63=makeQuery(id+"F0.imprint","IMPRINT",FACE,{"disambiguationData":[TD([[makeQuery(id+"F0.imprint","IMPRINT",EDGE,{"disambiguationData":[TD([[subQ2,-1.0]])],"derivedFrom":subQ1}),-1.0]])]});}
            var Q64;
            {var subQ0=sQuery(id+"F0.wireOp",EDGE,"E33.5.1");var subQ1=sQuery(id+"F0.wireOp",EDGE,"E14");var subQ2=makeQuery(id+"F0.imprint","INTERSECT",VERTEX,{"derivedFrom":[subQ1,subQ0]});Q64=makeQuery(id+"F0.imprint","IMPRINT",FACE,{"disambiguationData":[TD([[makeQuery(id+"F0.imprint","IMPRINT",EDGE,{"disambiguationData":[TD([[subQ2,-1.0]])],"derivedFrom":subQ1}),-1.0]])]});}
            var Q65;
            {var subQ0=sQuery(id+"F0.wireOp",EDGE,"E33.5.1");var subQ1=sQuery(id+"F0.wireOp",EDGE,"E16");var subQ2=makeQuery(id+"F0.imprint","INTERSECT",VERTEX,{"derivedFrom":[subQ1,subQ0]});Q65=makeQuery(id+"F0.imprint","IMPRINT",FACE,{"disambiguationData":[TD([[makeQuery(id+"F0.imprint","IMPRINT",EDGE,{"disambiguationData":[TD([[subQ2,-1.0]])],"derivedFrom":subQ1}),-1.0]])]});}
            var Q66;
            {var subQ0=sQuery(id+"F0.wireOp",EDGE,"E33.5.1");var subQ1=sQuery(id+"F0.wireOp",EDGE,"E24");var subQ2=makeQuery(id+"F0.imprint","INTERSECT",VERTEX,{"derivedFrom":[subQ1,subQ0]});Q66=makeQuery(id+"F0.imprint","IMPRINT",FACE,{"disambiguationData":[TD([[makeQuery(id+"F0.imprint","IMPRINT",EDGE,{"disambiguationData":[TD([[subQ2,-1.0]])],"derivedFrom":subQ1}),-1.0]])]});}
            var Q67;
            {var subQ0=sQuery(id+"F0.wireOp",EDGE,"E33.6.0");var subQ1=sQuery(id+"F0.wireOp",EDGE,"E10");var subQ2=makeQuery(id+"F0.imprint","INTERSECT",VERTEX,{"derivedFrom":[subQ1,subQ0]});Q67=makeQuery(id+"F0.imprint","IMPRINT",FACE,{"disambiguationData":[TD([[makeQuery(id+"F0.imprint","IMPRINT",EDGE,{"disambiguationData":[TD([[subQ2,-1.0]])],"derivedFrom":subQ1}),1.0]])]});}
            var Q68;
            {var subQ0=sQuery(id+"F0.wireOp",EDGE,"E33.6.0");var subQ1=sQuery(id+"F0.wireOp",EDGE,"E24");var subQ2=makeQuery(id+"F0.imprint","INTERSECT",VERTEX,{"derivedFrom":[subQ1,subQ0]});Q68=makeQuery(id+"F0.imprint","IMPRINT",FACE,{"disambiguationData":[TD([[makeQuery(id+"F0.imprint","IMPRINT",EDGE,{"disambiguationData":[TD([[subQ2,-1.0]])],"derivedFrom":subQ1}),-1.0]])]});}
            var Q69;
            {var subQ0=sQuery(id+"F0.wireOp",EDGE,"E33.6.0");var subQ1=sQuery(id+"F0.wireOp",EDGE,"E17");var subQ2=makeQuery(id+"F0.imprint","INTERSECT",VERTEX,{"derivedFrom":[subQ1,subQ0]});Q69=makeQuery(id+"F0.imprint","IMPRINT",FACE,{"disambiguationData":[TD([[makeQuery(id+"F0.imprint","IMPRINT",EDGE,{"disambiguationData":[TD([[subQ2,-1.0]])],"derivedFrom":subQ1}),-1.0]])]});}
            var Q70;
            {var subQ0=sQuery(id+"F0.wireOp",EDGE,"E33.6.0");var subQ1=sQuery(id+"F0.wireOp",EDGE,"E16");var subQ2=makeQuery(id+"F0.imprint","INTERSECT",VERTEX,{"derivedFrom":[subQ1,subQ0]});Q70=makeQuery(id+"F0.imprint","IMPRINT",FACE,{"disambiguationData":[TD([[makeQuery(id+"F0.imprint","IMPRINT",EDGE,{"disambiguationData":[TD([[subQ2,-1.0]])],"derivedFrom":subQ1}),-1.0]])]});}
            var Q71;
            {var subQ0=sQuery(id+"F0.wireOp",EDGE,"E33.6.0");var subQ1=sQuery(id+"F0.wireOp",EDGE,"E15");var subQ2=makeQuery(id+"F0.imprint","INTERSECT",VERTEX,{"derivedFrom":[subQ1,subQ0]});Q71=makeQuery(id+"F0.imprint","IMPRINT",FACE,{"disambiguationData":[TD([[makeQuery(id+"F0.imprint","IMPRINT",EDGE,{"disambiguationData":[TD([[subQ2,-1.0]])],"derivedFrom":subQ1}),-1.0]])]});}
            var Q72;
            {var subQ0=sQuery(id+"F0.wireOp",EDGE,"E33.6.0");var subQ1=sQuery(id+"F0.wireOp",EDGE,"E14");var subQ2=makeQuery(id+"F0.imprint","INTERSECT",VERTEX,{"derivedFrom":[subQ1,subQ0]});Q72=makeQuery(id+"F0.imprint","IMPRINT",FACE,{"disambiguationData":[TD([[makeQuery(id+"F0.imprint","IMPRINT",EDGE,{"disambiguationData":[TD([[subQ2,-1.0]])],"derivedFrom":subQ1}),-1.0]])]});}
            var Q73;
            {var subQ0=sQuery(id+"F0.wireOp",EDGE,"E33.6.0");var subQ1=sQuery(id+"F0.wireOp",EDGE,"E13");var subQ2=makeQuery(id+"F0.imprint","INTERSECT",VERTEX,{"derivedFrom":[subQ1,subQ0]});Q73=makeQuery(id+"F0.imprint","IMPRINT",FACE,{"disambiguationData":[TD([[makeQuery(id+"F0.imprint","IMPRINT",EDGE,{"disambiguationData":[TD([[subQ2,-1.0]])],"derivedFrom":subQ1}),-1.0]])]});}
            var Q74;
            {var subQ0=sQuery(id+"F0.wireOp",EDGE,"E33.6.0");var subQ1=sQuery(id+"F0.wireOp",EDGE,"E12");var subQ2=makeQuery(id+"F0.imprint","INTERSECT",VERTEX,{"derivedFrom":[subQ1,subQ0]});Q74=makeQuery(id+"F0.imprint","IMPRINT",FACE,{"disambiguationData":[TD([[makeQuery(id+"F0.imprint","IMPRINT",EDGE,{"disambiguationData":[TD([[subQ2,-1.0]])],"derivedFrom":subQ1}),-1.0]])]});}
            var Q75;
            {var subQ0=sQuery(id+"F0.wireOp",EDGE,"E33.6.0");var subQ1=sQuery(id+"F0.wireOp",EDGE,"E11");var subQ2=makeQuery(id+"F0.imprint","INTERSECT",VERTEX,{"derivedFrom":[subQ1,subQ0]});Q75=makeQuery(id+"F0.imprint","IMPRINT",FACE,{"disambiguationData":[TD([[makeQuery(id+"F0.imprint","IMPRINT",EDGE,{"disambiguationData":[TD([[subQ2,-1.0]])],"derivedFrom":subQ1}),-1.0]])]});}
            var Q76;
            {var subQ0=sQuery(id+"F0.wireOp",EDGE,"E33.6.1");var subQ1=sQuery(id+"F0.wireOp",EDGE,"E12");var subQ2=makeQuery(id+"F0.imprint","INTERSECT",VERTEX,{"derivedFrom":[subQ1,subQ0]});Q76=makeQuery(id+"F0.imprint","IMPRINT",FACE,{"disambiguationData":[TD([[makeQuery(id+"F0.imprint","IMPRINT",EDGE,{"disambiguationData":[TD([[subQ2,-1.0]])],"derivedFrom":subQ1}),-1.0]])]});}
            var Q77;
            {var subQ0=sQuery(id+"F0.wireOp",EDGE,"E33.6.1");var subQ1=sQuery(id+"F0.wireOp",EDGE,"E14");var subQ2=makeQuery(id+"F0.imprint","INTERSECT",VERTEX,{"derivedFrom":[subQ1,subQ0]});Q77=makeQuery(id+"F0.imprint","IMPRINT",FACE,{"disambiguationData":[TD([[makeQuery(id+"F0.imprint","IMPRINT",EDGE,{"disambiguationData":[TD([[subQ2,-1.0]])],"derivedFrom":subQ1}),-1.0]])]});}
            var Q78;
            {var subQ0=sQuery(id+"F0.wireOp",EDGE,"E33.6.1");var subQ1=sQuery(id+"F0.wireOp",EDGE,"E16");var subQ2=makeQuery(id+"F0.imprint","INTERSECT",VERTEX,{"derivedFrom":[subQ1,subQ0]});Q78=makeQuery(id+"F0.imprint","IMPRINT",FACE,{"disambiguationData":[TD([[makeQuery(id+"F0.imprint","IMPRINT",EDGE,{"disambiguationData":[TD([[subQ2,-1.0]])],"derivedFrom":subQ1}),-1.0]])]});}
            var Q79;
            {var subQ0=sQuery(id+"F0.wireOp",EDGE,"E33.6.1");var subQ1=sQuery(id+"F0.wireOp",EDGE,"E24");var subQ2=makeQuery(id+"F0.imprint","INTERSECT",VERTEX,{"derivedFrom":[subQ1,subQ0]});Q79=makeQuery(id+"F0.imprint","IMPRINT",FACE,{"disambiguationData":[TD([[makeQuery(id+"F0.imprint","IMPRINT",EDGE,{"disambiguationData":[TD([[subQ2,-1.0]])],"derivedFrom":subQ1}),-1.0]])]});}
            var Q80;
            {var subQ0=sQuery(id+"F0.wireOp",EDGE,"E33.7.0");var subQ1=sQuery(id+"F0.wireOp",EDGE,"E10");var subQ2=makeQuery(id+"F0.imprint","INTERSECT",VERTEX,{"derivedFrom":[subQ1,subQ0]});Q80=makeQuery(id+"F0.imprint","IMPRINT",FACE,{"disambiguationData":[TD([[makeQuery(id+"F0.imprint","IMPRINT",EDGE,{"disambiguationData":[TD([[subQ2,-1.0]])],"derivedFrom":subQ1}),1.0]])]});}
            var Q81;
            {var subQ0=sQuery(id+"F0.wireOp",EDGE,"E33.7.0");var subQ1=sQuery(id+"F0.wireOp",EDGE,"E24");var subQ2=makeQuery(id+"F0.imprint","INTERSECT",VERTEX,{"derivedFrom":[subQ1,subQ0]});Q81=makeQuery(id+"F0.imprint","IMPRINT",FACE,{"disambiguationData":[TD([[makeQuery(id+"F0.imprint","IMPRINT",EDGE,{"disambiguationData":[TD([[subQ2,-1.0]])],"derivedFrom":subQ1}),-1.0]])]});}
            var Q82;
            {var subQ0=sQuery(id+"F0.wireOp",EDGE,"E33.7.0");var subQ1=sQuery(id+"F0.wireOp",EDGE,"E17");var subQ2=makeQuery(id+"F0.imprint","INTERSECT",VERTEX,{"derivedFrom":[subQ1,subQ0]});Q82=makeQuery(id+"F0.imprint","IMPRINT",FACE,{"disambiguationData":[TD([[makeQuery(id+"F0.imprint","IMPRINT",EDGE,{"disambiguationData":[TD([[subQ2,-1.0]])],"derivedFrom":subQ1}),-1.0]])]});}
            var Q83;
            {var subQ0=sQuery(id+"F0.wireOp",EDGE,"E33.7.0");var subQ1=sQuery(id+"F0.wireOp",EDGE,"E16");var subQ2=makeQuery(id+"F0.imprint","INTERSECT",VERTEX,{"derivedFrom":[subQ1,subQ0]});Q83=makeQuery(id+"F0.imprint","IMPRINT",FACE,{"disambiguationData":[TD([[makeQuery(id+"F0.imprint","IMPRINT",EDGE,{"disambiguationData":[TD([[subQ2,-1.0]])],"derivedFrom":subQ1}),-1.0]])]});}
            var Q84;
            {var subQ0=sQuery(id+"F0.wireOp",EDGE,"E33.7.0");var subQ1=sQuery(id+"F0.wireOp",EDGE,"E15");var subQ2=makeQuery(id+"F0.imprint","INTERSECT",VERTEX,{"derivedFrom":[subQ1,subQ0]});Q84=makeQuery(id+"F0.imprint","IMPRINT",FACE,{"disambiguationData":[TD([[makeQuery(id+"F0.imprint","IMPRINT",EDGE,{"disambiguationData":[TD([[subQ2,-1.0]])],"derivedFrom":subQ1}),-1.0]])]});}
            var Q85;
            {var subQ0=sQuery(id+"F0.wireOp",EDGE,"E33.7.0");var subQ1=sQuery(id+"F0.wireOp",EDGE,"E14");var subQ2=makeQuery(id+"F0.imprint","INTERSECT",VERTEX,{"derivedFrom":[subQ1,subQ0]});Q85=makeQuery(id+"F0.imprint","IMPRINT",FACE,{"disambiguationData":[TD([[makeQuery(id+"F0.imprint","IMPRINT",EDGE,{"disambiguationData":[TD([[subQ2,-1.0]])],"derivedFrom":subQ1}),-1.0]])]});}
            var Q86;
            {var subQ0=sQuery(id+"F0.wireOp",EDGE,"E33.7.0");var subQ1=sQuery(id+"F0.wireOp",EDGE,"E13");var subQ2=makeQuery(id+"F0.imprint","INTERSECT",VERTEX,{"derivedFrom":[subQ1,subQ0]});Q86=makeQuery(id+"F0.imprint","IMPRINT",FACE,{"disambiguationData":[TD([[makeQuery(id+"F0.imprint","IMPRINT",EDGE,{"disambiguationData":[TD([[subQ2,-1.0]])],"derivedFrom":subQ1}),-1.0]])]});}
            var Q87;
            {var subQ0=sQuery(id+"F0.wireOp",EDGE,"E33.7.0");var subQ1=sQuery(id+"F0.wireOp",EDGE,"E12");var subQ2=makeQuery(id+"F0.imprint","INTERSECT",VERTEX,{"derivedFrom":[subQ1,subQ0]});Q87=makeQuery(id+"F0.imprint","IMPRINT",FACE,{"disambiguationData":[TD([[makeQuery(id+"F0.imprint","IMPRINT",EDGE,{"disambiguationData":[TD([[subQ2,-1.0]])],"derivedFrom":subQ1}),-1.0]])]});}
            var Q88;
            {var subQ0=sQuery(id+"F0.wireOp",EDGE,"E33.7.0");var subQ1=sQuery(id+"F0.wireOp",EDGE,"E11");var subQ2=makeQuery(id+"F0.imprint","INTERSECT",VERTEX,{"derivedFrom":[subQ1,subQ0]});Q88=makeQuery(id+"F0.imprint","IMPRINT",FACE,{"disambiguationData":[TD([[makeQuery(id+"F0.imprint","IMPRINT",EDGE,{"disambiguationData":[TD([[subQ2,-1.0]])],"derivedFrom":subQ1}),-1.0]])]});}
            var Q89;
            {var subQ0=sQuery(id+"F0.wireOp",EDGE,"E29");var subQ1=sQuery(id+"F0.wireOp",EDGE,"E10");var subQ2=makeQuery(id+"F0.imprint","INTERSECT",VERTEX,{"derivedFrom":[subQ1,subQ0]});Q89=makeQuery(id+"F0.imprint","IMPRINT",FACE,{"disambiguationData":[TD([[makeQuery(id+"F0.imprint","IMPRINT",EDGE,{"disambiguationData":[TD([[subQ2,-1.0]])],"derivedFrom":subQ1}),1.0]])]});}
            var Q90;
            {var subQ0=sQuery(id+"F0.wireOp",EDGE,"E29");var subQ1=sQuery(id+"F0.wireOp",EDGE,"E24");var subQ2=makeQuery(id+"F0.imprint","INTERSECT",VERTEX,{"derivedFrom":[subQ1,subQ0]});Q90=makeQuery(id+"F0.imprint","IMPRINT",FACE,{"disambiguationData":[TD([[makeQuery(id+"F0.imprint","IMPRINT",EDGE,{"disambiguationData":[TD([[subQ2,-1.0]])],"derivedFrom":subQ1}),-1.0]])]});}
            var Q91;
            {var subQ0=sQuery(id+"F0.wireOp",EDGE,"E29");var subQ1=sQuery(id+"F0.wireOp",EDGE,"E17");var subQ2=makeQuery(id+"F0.imprint","INTERSECT",VERTEX,{"derivedFrom":[subQ1,subQ0]});Q91=makeQuery(id+"F0.imprint","IMPRINT",FACE,{"disambiguationData":[TD([[makeQuery(id+"F0.imprint","IMPRINT",EDGE,{"disambiguationData":[TD([[subQ2,-1.0]])],"derivedFrom":subQ1}),-1.0]])]});}
            var Q92;
            {var subQ0=sQuery(id+"F0.wireOp",EDGE,"E29");var subQ1=sQuery(id+"F0.wireOp",EDGE,"E16");var subQ2=makeQuery(id+"F0.imprint","INTERSECT",VERTEX,{"derivedFrom":[subQ1,subQ0]});Q92=makeQuery(id+"F0.imprint","IMPRINT",FACE,{"disambiguationData":[TD([[makeQuery(id+"F0.imprint","IMPRINT",EDGE,{"disambiguationData":[TD([[subQ2,-1.0]])],"derivedFrom":subQ1}),-1.0]])]});}
            var Q93;
            {var subQ0=sQuery(id+"F0.wireOp",EDGE,"E29");var subQ1=sQuery(id+"F0.wireOp",EDGE,"E15");var subQ2=makeQuery(id+"F0.imprint","INTERSECT",VERTEX,{"derivedFrom":[subQ1,subQ0]});Q93=makeQuery(id+"F0.imprint","IMPRINT",FACE,{"disambiguationData":[TD([[makeQuery(id+"F0.imprint","IMPRINT",EDGE,{"disambiguationData":[TD([[subQ2,-1.0]])],"derivedFrom":subQ1}),-1.0]])]});}
            var Q94;
            {var subQ0=sQuery(id+"F0.wireOp",EDGE,"E29");var subQ1=sQuery(id+"F0.wireOp",EDGE,"E14");var subQ2=makeQuery(id+"F0.imprint","INTERSECT",VERTEX,{"derivedFrom":[subQ1,subQ0]});Q94=makeQuery(id+"F0.imprint","IMPRINT",FACE,{"disambiguationData":[TD([[makeQuery(id+"F0.imprint","IMPRINT",EDGE,{"disambiguationData":[TD([[subQ2,-1.0]])],"derivedFrom":subQ1}),-1.0]])]});}
            var Q95;
            {var subQ0=sQuery(id+"F0.wireOp",EDGE,"E29");var subQ1=sQuery(id+"F0.wireOp",EDGE,"E13");var subQ2=makeQuery(id+"F0.imprint","INTERSECT",VERTEX,{"derivedFrom":[subQ1,subQ0]});Q95=makeQuery(id+"F0.imprint","IMPRINT",FACE,{"disambiguationData":[TD([[makeQuery(id+"F0.imprint","IMPRINT",EDGE,{"disambiguationData":[TD([[subQ2,-1.0]])],"derivedFrom":subQ1}),-1.0]])]});}
            var Q96;
            {var subQ0=sQuery(id+"F0.wireOp",EDGE,"E29");var subQ1=sQuery(id+"F0.wireOp",EDGE,"E12");var subQ2=makeQuery(id+"F0.imprint","INTERSECT",VERTEX,{"derivedFrom":[subQ1,subQ0]});Q96=makeQuery(id+"F0.imprint","IMPRINT",FACE,{"disambiguationData":[TD([[makeQuery(id+"F0.imprint","IMPRINT",EDGE,{"disambiguationData":[TD([[subQ2,-1.0]])],"derivedFrom":subQ1}),-1.0]])]});}
            var Q97;
            {var subQ0=sQuery(id+"F0.wireOp",EDGE,"E29");var subQ1=sQuery(id+"F0.wireOp",EDGE,"E11");var subQ2=makeQuery(id+"F0.imprint","INTERSECT",VERTEX,{"derivedFrom":[subQ1,subQ0]});Q97=makeQuery(id+"F0.imprint","IMPRINT",FACE,{"disambiguationData":[TD([[makeQuery(id+"F0.imprint","IMPRINT",EDGE,{"disambiguationData":[TD([[subQ2,-1.0]])],"derivedFrom":subQ1}),-1.0]])]});}
            var Q98;
            {var subQ0=sQuery(id+"F0.wireOp",EDGE,"E33.7.1");var subQ1=sQuery(id+"F0.wireOp",EDGE,"E12");var subQ2=makeQuery(id+"F0.imprint","INTERSECT",VERTEX,{"derivedFrom":[subQ1,subQ0]});Q98=makeQuery(id+"F0.imprint","IMPRINT",FACE,{"disambiguationData":[TD([[makeQuery(id+"F0.imprint","IMPRINT",EDGE,{"disambiguationData":[TD([[subQ2,-1.0]])],"derivedFrom":subQ1}),-1.0]])]});}
            var Q99;
            {var subQ0=sQuery(id+"F0.wireOp",EDGE,"E33.7.1");var subQ1=sQuery(id+"F0.wireOp",EDGE,"E14");var subQ2=makeQuery(id+"F0.imprint","INTERSECT",VERTEX,{"derivedFrom":[subQ1,subQ0]});Q99=makeQuery(id+"F0.imprint","IMPRINT",FACE,{"disambiguationData":[TD([[makeQuery(id+"F0.imprint","IMPRINT",EDGE,{"disambiguationData":[TD([[subQ2,-1.0]])],"derivedFrom":subQ1}),-1.0]])]});}
            var Q100;
            {var subQ0=sQuery(id+"F0.wireOp",EDGE,"E33.7.1");var subQ1=sQuery(id+"F0.wireOp",EDGE,"E16");var subQ2=makeQuery(id+"F0.imprint","INTERSECT",VERTEX,{"derivedFrom":[subQ1,subQ0]});Q100=makeQuery(id+"F0.imprint","IMPRINT",FACE,{"disambiguationData":[TD([[makeQuery(id+"F0.imprint","IMPRINT",EDGE,{"disambiguationData":[TD([[subQ2,-1.0]])],"derivedFrom":subQ1}),-1.0]])]});}
            var Q101;
            {var subQ0=sQuery(id+"F0.wireOp",EDGE,"E33.7.1");var subQ1=sQuery(id+"F0.wireOp",EDGE,"E24");var subQ2=makeQuery(id+"F0.imprint","INTERSECT",VERTEX,{"derivedFrom":[subQ1,subQ0]});Q101=makeQuery(id+"F0.imprint","IMPRINT",FACE,{"disambiguationData":[TD([[makeQuery(id+"F0.imprint","IMPRINT",EDGE,{"disambiguationData":[TD([[subQ2,-1.0]])],"derivedFrom":subQ1}),-1.0]])]});}
            var Q102;
            {var subQ0=sQuery(id+"F0.wireOp",EDGE,"E30");var subQ1=sQuery(id+"F0.wireOp",EDGE,"E24");var subQ2=makeQuery(id+"F0.imprint","INTERSECT",VERTEX,{"derivedFrom":[subQ1,subQ0]});Q102=makeQuery(id+"F0.imprint","IMPRINT",FACE,{"disambiguationData":[TD([[makeQuery(id+"F0.imprint","IMPRINT",EDGE,{"disambiguationData":[TD([[subQ2,-1.0]])],"derivedFrom":subQ1}),-1.0]])]});}
            var Q103;
            {var subQ0=sQuery(id+"F0.wireOp",EDGE,"E30");var subQ1=sQuery(id+"F0.wireOp",EDGE,"E16");var subQ2=makeQuery(id+"F0.imprint","INTERSECT",VERTEX,{"derivedFrom":[subQ1,subQ0]});Q103=makeQuery(id+"F0.imprint","IMPRINT",FACE,{"disambiguationData":[TD([[makeQuery(id+"F0.imprint","IMPRINT",EDGE,{"disambiguationData":[TD([[subQ2,-1.0]])],"derivedFrom":subQ1}),-1.0]])]});}
            var Q104;
            {var subQ0=sQuery(id+"F0.wireOp",EDGE,"E30");var subQ1=sQuery(id+"F0.wireOp",EDGE,"E14");var subQ2=makeQuery(id+"F0.imprint","INTERSECT",VERTEX,{"derivedFrom":[subQ1,subQ0]});Q104=makeQuery(id+"F0.imprint","IMPRINT",FACE,{"disambiguationData":[TD([[makeQuery(id+"F0.imprint","IMPRINT",EDGE,{"disambiguationData":[TD([[subQ2,-1.0]])],"derivedFrom":subQ1}),-1.0]])]});}
            var Q105;
            {var subQ0=sQuery(id+"F0.wireOp",EDGE,"E30");var subQ1=sQuery(id+"F0.wireOp",EDGE,"E12");var subQ2=makeQuery(id+"F0.imprint","INTERSECT",VERTEX,{"derivedFrom":[subQ1,subQ0]});Q105=makeQuery(id+"F0.imprint","IMPRINT",FACE,{"disambiguationData":[TD([[makeQuery(id+"F0.imprint","IMPRINT",EDGE,{"disambiguationData":[TD([[subQ2,-1.0]])],"derivedFrom":subQ1}),-1.0]])]});}
            extrude(context, id + "F1", {"entities" : qUnion([Q0, Q1, Q2, Q3, Q4, Q5, Q6, Q7, Q8, Q9, Q10, Q11, Q12, Q13, Q14, Q15, Q16, Q17, Q18, Q19, Q20, Q21, Q22, Q23, Q24, Q25, Q26, Q27, Q28, Q29, Q30, Q31, Q32, Q33, Q34, Q35, Q36, Q37, Q38, Q39, Q40, Q41, Q42, Q43, Q44, Q45, Q46, Q47, Q48, Q49, Q50, Q51, Q52, Q53, Q54, Q55, Q56, Q57, Q58, Q59, Q60, Q61, Q62, Q63, Q64, Q65, Q66, Q67, Q68, Q69, Q70, Q71, Q72, Q73, Q74, Q75, Q76, Q77, Q78, Q79, Q80, Q81, Q82, Q83, Q84, Q85, Q86, Q87, Q88, Q89, Q90, Q91, Q92, Q93, Q94, Q95, Q96, Q97, Q98, Q99, Q100, Q101, Q102, Q103, Q104, Q105]), "depth" : 1 / 101.6 * mm, "offsetDistance" : 25 * mm});
        }
        {
            var Q0;
            Q0=qCreatedBy(makeId("Top.planeOp"),FACE);
            var sketch = newSketch(context, id + "F2", { "sketchPlane" : qUnion([Q0])});
            skLineSegment(sketch, "E34.0", {"start": v(6.35, 57.94) * mm, "end": v(6.35, 53.33) * mm});
            skLineSegment(sketch, "E35.0", {"start": v(6.35, -53.33) * mm, "end": v(6.35, -57.94) * mm});
            skLineSegment(sketch, "E36", {"start": v(0, 0) * mm, "end": v(3.18, 0) * mm, "construction": true});
            skLineSegment(sketch, "E37", {"start": v(0, 0) * mm, "end": v(-55.23, 0) * mm, "construction": true});
            skArc(sketch, "E38", {"start": v(6.35, 57.94) * mm, "mid": v(3.97, 29.02) * mm, "end": v(3.17, 0) * mm});
            skLineSegment(sketch, "E39", {"start": v(3.18, 0) * mm, "end": v(3.18, -6.38) * mm, "construction": true});
            skLineSegment(sketch, "E40", {"start": v(3.18, 0) * mm, "end": v(6.35, 0) * mm});
            skLineSegment(sketch, "E41", {"start": v(6.35, 0) * mm, "end": v(6.35, 53.33) * mm});
            skSolve(sketch);
        }
        {
            var Q0;
            Q0 = qSketchRegion(id + "F2", true);
            var Q1;
            Q1=sQuery(id+"F2.wireOp",EDGE,"E37");
            revolve(context, id + "F3", {"operationType" : NewBodyOperationType.REMOVE, "entities" : qUnion([Q0]), "axis" : qUnion([Q1]), "revolveType" : RevolveType.FULL, "oppositeDirection" : true});
        }
        {
            var Q0;
            Q0=makeQuery(id+"F1.opExtrude","CAP_FACE",FACE,{"disambiguationData":[OSD([sQuery(id+"F0.wireOp",EDGE,"E0.bottom"),sQuery(id+"F0.wireOp",EDGE,"E0.top"),sQuery(id+"F0.wireOp",EDGE,"E0.left"),sQuery(id+"F0.wireOp",EDGE,"E0.right"),sQuery(id+"F0.wireOp",EDGE,"E1.filletArc"),sQuery(id+"F0.wireOp",EDGE,"E2.filletArc"),sQuery(id+"F0.wireOp",EDGE,"E3.filletArc"),sQuery(id+"F0.wireOp",EDGE,"E4.filletArc"),sQuery(id+"F0.wireOp",EDGE,"E6"),sQuery(id+"F0.wireOp",EDGE,"E7"),sQuery(id+"F0.wireOp",EDGE,"E8"),sQuery(id+"F0.wireOp",EDGE,"E9"),sQuery(id+"F0.wireOp",EDGE,"E10"),sQuery(id+"F0.wireOp",EDGE,"E11"),sQuery(id+"F0.wireOp",EDGE,"E12"),sQuery(id+"F0.wireOp",EDGE,"E13"),sQuery(id+"F0.wireOp",EDGE,"E14"),sQuery(id+"F0.wireOp",EDGE,"E15"),sQuery(id+"F0.wireOp",EDGE,"E16"),sQuery(id+"F0.wireOp",EDGE,"E17"),sQuery(id+"F0.wireOp",EDGE,"E24"),sQuery(id+"F0.wireOp",EDGE,"E25"),sQuery(id+"F0.wireOp",EDGE,"E29"),sQuery(id+"F0.wireOp",EDGE,"E30"),sQuery(id+"F0.wireOp",EDGE,"E33.1.0"),sQuery(id+"F0.wireOp",EDGE,"E33.1.1"),sQuery(id+"F0.wireOp",EDGE,"E33.2.0"),sQuery(id+"F0.wireOp",EDGE,"E33.2.1"),sQuery(id+"F0.wireOp",EDGE,"E33.3.0"),sQuery(id+"F0.wireOp",EDGE,"E33.3.1"),sQuery(id+"F0.wireOp",EDGE,"E33.4.0"),sQuery(id+"F0.wireOp",EDGE,"E33.4.1"),sQuery(id+"F0.wireOp",EDGE,"E33.5.0"),sQuery(id+"F0.wireOp",EDGE,"E33.5.1"),sQuery(id+"F0.wireOp",EDGE,"E33.6.0"),sQuery(id+"F0.wireOp",EDGE,"E33.6.1"),sQuery(id+"F0.wireOp",EDGE,"E33.7.0"),sQuery(id+"F0.wireOp",EDGE,"E33.7.1")])],"isStart":false});
            var sketch = newSketch(context, id + "F4", { "sketchPlane" : qUnion([Q0])});
            skLineSegment(sketch, "E42", {"start": v(-56.19, 46.6) * mm, "end": v(-52.5, 46.6) * mm});
            skLineSegment(sketch, "E43", {"start": v(-46.6, 52.5) * mm, "end": v(-46.6, 56.19) * mm});
            skLineSegment(sketch, "E44", {"start": v(-46.6, 56.19) * mm, "end": v(-25.7, 56.19) * mm});
            skArc(sketch, "E45", {"start": v(-25.7, 56.19) * mm, "mid": v(-43.69, 43.69) * mm, "end": v(-56.19, 25.7) * mm});
            skLineSegment(sketch, "E46", {"start": v(-56.19, 46.6) * mm, "end": v(-56.19, 25.7) * mm});
            skLineSegment(sketch, "E47", {"start": v(-52.5, 52.5) * mm, "end": v(-46.6, 52.5) * mm, "construction": true});
            skPoint(sketch, "E48.visualSharp", {"position": v(-46.6, 46.6) * mm});
            skArc(sketch, "E48.filletArc", {"start": v(-52.5, 46.6) * mm, "mid": v(-48.32, 48.32) * mm, "end": v(-46.6, 52.5) * mm});
            skSolve(sketch);
        }
        {
            var Q0;
            Q0=makeQuery(id+"F4.imprint","IMPRINT",FACE,{"disambiguationData":[TD([[makeQuery(id+"F4.imprint","IMPRINT",EDGE,{"derivedFrom":sQuery(id+"F4.wireOp",EDGE,"E42")}),-1.0]])]});
            extrude(context, id + "F5", {"entities" : qUnion([Q0]), "operationType" : NewBodyOperationType.REMOVE, "oppositeDirection" : true, "depth" : 1 / 203.2 * mm, "offsetDistance" : 25 * mm});
        }
    });
